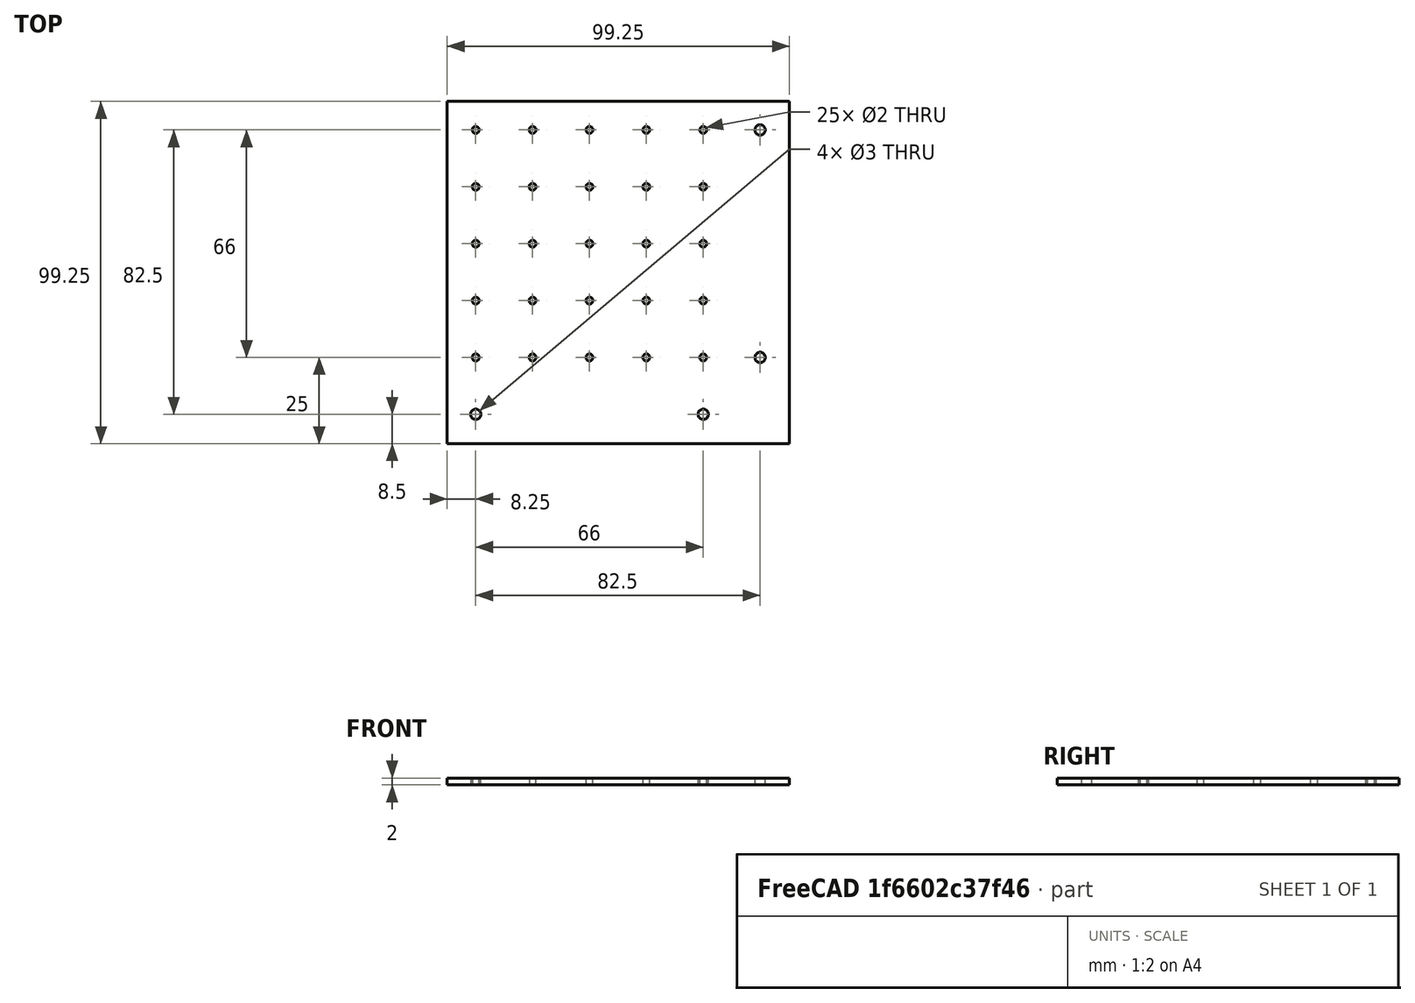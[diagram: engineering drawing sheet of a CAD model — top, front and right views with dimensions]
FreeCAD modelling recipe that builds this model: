
FCSTD DOCUMENT  (FreeCAD 0.21R33771 (Git))
Label: led_matrix_drill_frame
License: All rights reserved
LicenseURL: http://en.wikipedia.org/wiki/All_rights_reserved
objects: Sketcher::SketchObject×1, PartDesign::Pad×1, PartDesign::Body×1
note: 4 computed .brp shape members not serialized (recipe doc carries the construction recipe); baked Part::Feature solids carry a one-line shape summary decoded from their .brp

FEATURE [Sketcher::SketchObject] Sketch
  FullyConstrained = true
  MapMode = 5
  Support = -> [XY_Plane]
  sketch-geometry (37):
    g0: GeomPoint X=0 Y=0 Z=0
    g1: Circle CenterX=0 CenterY=0 CenterZ=0 NormalX=0 NormalY=0 NormalZ=1 AngleXU=0 Radius=1
    g2: Circle CenterX=-16.5 CenterY=0 CenterZ=0 NormalX=0 NormalY=0 NormalZ=1 AngleXU=0 Radius=1
    g3: GeomPoint X=4e-16 Y=16.5 Z=0
    g4: Circle CenterX=4e-16 CenterY=16.5 CenterZ=0 NormalX=0 NormalY=0 NormalZ=1 AngleXU=0 Radius=1
    g5: Circle CenterX=-16.5 CenterY=16.5 CenterZ=0 NormalX=0 NormalY=0 NormalZ=1 AngleXU=0 Radius=1
    g6: GeomPoint X=-33 Y=16.5 Z=0
    g7: Circle CenterX=-33 CenterY=16.5 CenterZ=0 NormalX=0 NormalY=0 NormalZ=1 AngleXU=0 Radius=1
    g8: GeomPoint X=33 Y=16.5 Z=0
    g9: Circle CenterX=33 CenterY=16.5 CenterZ=0 NormalX=0 NormalY=0 NormalZ=1 AngleXU=0 Radius=1
    g10: Circle CenterX=16.5 CenterY=16.5 CenterZ=0 NormalX=0 NormalY=0 NormalZ=1 AngleXU=0 Radius=1
    g11: Circle CenterX=-33 CenterY=0 CenterZ=0 NormalX=0 NormalY=0 NormalZ=1 AngleXU=0 Radius=1
    g12: Circle CenterX=16.5 CenterY=0 CenterZ=0 NormalX=0 NormalY=0 NormalZ=1 AngleXU=0 Radius=1
    g13: Circle CenterX=33 CenterY=0 CenterZ=0 NormalX=0 NormalY=0 NormalZ=1 AngleXU=0 Radius=1
    g14: Circle CenterX=0 CenterY=-16.5 CenterZ=0 NormalX=0 NormalY=0 NormalZ=1 AngleXU=0 Radius=1
    g15: Circle CenterX=16.5 CenterY=-16.5 CenterZ=0 NormalX=0 NormalY=0 NormalZ=1 AngleXU=0 Radius=1
    g16: Circle CenterX=33 CenterY=-16.5 CenterZ=0 NormalX=0 NormalY=0 NormalZ=1 AngleXU=0 Radius=1
    g17: Circle CenterX=-16.5 CenterY=-16.5 CenterZ=0 NormalX=0 NormalY=0 NormalZ=1 AngleXU=0 Radius=1
    g18: Circle CenterX=-33 CenterY=-16.5 CenterZ=0 NormalX=0 NormalY=0 NormalZ=1 AngleXU=0 Radius=1
    g19: Circle CenterX=-33 CenterY=33 CenterZ=0 NormalX=0 NormalY=0 NormalZ=1 AngleXU=0 Radius=1
    g20: Circle CenterX=-16.5 CenterY=33 CenterZ=0 NormalX=0 NormalY=0 NormalZ=1 AngleXU=0 Radius=1
    g21: Circle CenterX=0 CenterY=33 CenterZ=0 NormalX=0 NormalY=0 NormalZ=1 AngleXU=0 Radius=1
    g22: Circle CenterX=16.5 CenterY=33 CenterZ=0 NormalX=0 NormalY=0 NormalZ=1 AngleXU=0 Radius=1
    g23: Circle CenterX=33 CenterY=33 CenterZ=0 NormalX=0 NormalY=0 NormalZ=1 AngleXU=0 Radius=1
    g24: Circle CenterX=-33 CenterY=-33 CenterZ=0 NormalX=0 NormalY=0 NormalZ=1 AngleXU=0 Radius=1
    g25: Circle CenterX=-16.5 CenterY=-33 CenterZ=0 NormalX=0 NormalY=0 NormalZ=1 AngleXU=0 Radius=1
    g26: Circle CenterX=16.5 CenterY=-33 CenterZ=0 NormalX=0 NormalY=0 NormalZ=1 AngleXU=0 Radius=1
    g27: Circle CenterX=33 CenterY=-33 CenterZ=0 NormalX=0 NormalY=0 NormalZ=1 AngleXU=0 Radius=1
    g28: Circle CenterX=0 CenterY=-33 CenterZ=0 NormalX=0 NormalY=0 NormalZ=1 AngleXU=0 Radius=1
    g29: Circle CenterX=-33 CenterY=-49.5 CenterZ=0 NormalX=0 NormalY=0 NormalZ=1 AngleXU=0 Radius=1.5
    g30: Circle CenterX=33 CenterY=-49.5 CenterZ=0 NormalX=0 NormalY=0 NormalZ=1 AngleXU=0 Radius=1.5
    g31: Circle CenterX=49.5 CenterY=33 CenterZ=0 NormalX=0 NormalY=0 NormalZ=1 AngleXU=0 Radius=1.5
    g32: Circle CenterX=49.5 CenterY=-33 CenterZ=0 NormalX=0 NormalY=0 NormalZ=1 AngleXU=0 Radius=1.5
    g33: LineSegment StartX=-41.25 StartY=41.25 StartZ=0 EndX=58 EndY=41.25 EndZ=0
    g34: LineSegment StartX=58 StartY=41.25 StartZ=0 EndX=58 EndY=-58 EndZ=0
    g35: LineSegment StartX=58 StartY=-58 StartZ=0 EndX=-41.25 EndY=-58 EndZ=0
    g36: LineSegment StartX=-41.25 StartY=-58 StartZ=0 EndX=-41.25 EndY=41.25 EndZ=0
  constraints (102):
    c: Coincident(g0,g-1)
    c: Coincident(g1,g0)
    c: Diameter(g1) = 2
    c: PointOnObject(g2,g-1)
    c: Diameter(g2) = 2
    c: Distance(g2,g1) = 16.5
    c: Coincident(g4,g3)
    c: Equal(g1,g4) = 2
    c: Equal(g2,g5) = 2
    c: Distance(g5,g4) = 16.5
    c: Coincident(g7,g6)
    c: Equal(g4,g7) = 2
    c: Distance(g7,g5) = 16.5
    c: Coincident(g9,g8)
    c: Distance(g10,g9) = 16.5
    c: Distance(g10,g4) = 16.5
    c: Distance(g4,g-1) = 16.5
    c: Distance(g5,g-1) = 16.5
    c: Distance(g7,g-1) = 16.5
    c: Distance(g9,g-1) = 16.5
    c: Distance(g10,g-1) = 16.5
    c: Diameter(g10) = 2
    c: Diameter(g9) = 2
    c: PointOnObject(g11,g-1)
    c: Diameter(g11) = 2
    c: Distance(g11,g2) = 16.5
    c: PointOnObject(g12,g-1)
    c: Diameter(g12) = 2
    c: Distance(g12,g-2) = 16.5
    c: PointOnObject(g13,g-1)
    c: Diameter(g13) = 2
    c: Distance(g13,g12) = 16.5
    c: PointOnObject(g14,g-2)
    c: Diameter(g14) = 2
    c: Distance(g14,g1) = 16.5
    c: PointOnObject(g21,g-2)
    c: Diameter(g19) = 2
    c: Diameter(g20) = 2
    c: Diameter(g21) = 2
    c: Diameter(g22) = 2
    c: Diameter(g23) = 2
    c: Diameter(g18) = 2
    c: Diameter(g17) = 2
    c: Diameter(g15) = 2
    c: Diameter(g16) = 2
    c: Diameter(g27) = 2
    c: Diameter(g26) = 2
    c: Diameter(g25) = 2
    c: Diameter(g24) = 2
    c: PointOnObject(g28,g-2)
    c: Diameter(g28) = 2
    c: Distance(g17,g-1) = 16.5
    c: Distance(g17,g-2) = 16.5
    c: Distance(g18,g-1) = 16.5
    c: Distance(g18,g17) = 16.5
    c: Distance(g15,g-2) = 16.5
    c: Distance(g15,g-1) = 16.5
    c: Distance(g16,g-1) = 16.5
    c: Distance(g16,g15) = 16.5
    c: Distance(g28,g14) = 16.5
    c: Distance(g26,g28) = 16.5
    c: Distance(g26,g15) = 16.5
    c: Distance(g27,g26) = 16.5
    c: Distance(g27,g16) = 16.5
    c: Distance(g25,g28) = 16.5
    c: Distance(g25,g17) = 16.5
    c: Distance(g24,g25) = 16.5
    c: Distance(g24,g18) = 16.5
    c: Distance(g19,g7) = 16.5
    c: Distance(g21,g4) = 16.5
    c: Distance(g20,g5) = 16.5
    c: Distance(g20,g-2) = 16.5
    c: Distance(g19,g20) = 16.5
    c: Distance(g22,g10) = 16.5
    c: Distance(g22,g21) = 16.5
    c: Distance(g23,g9) = 16.5
    c: Distance(g23,g22) = 16.5
    c: Distance(g7,g-2) = 33
    c: Diameter(g31) = 3
    c: Diameter(g32) = 3
    c: Diameter(g30) = 3
    c: Diameter(g29) = 3
    c: Distance(g29,g-2) = 33
    c: Distance(g29,g24) = 16.5
    c: Distance(g30,g-2) = 33
    c: Distance(g30,g27) = 16.5
    c: Distance(g32,g-1) = 33
    c: Distance(g32,g27) = 16.5
    c: Distance(g31,g-1) = 33
    c: Distance(g31,g23) = 16.5
    c: Coincident(g33,g34)
    c: Coincident(g34,g35)
    c: Coincident(g35,g36)
    c: Coincident(g36,g33)
    c: Horizontal(g33)
    c: Horizontal(g35)
    c: Vertical(g34)
    c: Vertical(g36)
    c: Distance(g35,g-2) = 41.25
    c: Distance(g33,g-1) = 41.25
    c: Distance(g34,g-2) = 58
    c: Distance(g34,g-1) = 58
FEATURE [PartDesign::Pad] Pad
  Direction = (0,0,1)
  Length = 2
  Length2 = 10
  Profile = -> Sketch
  ReferenceAxis = -> Sketch [N_Axis]
  Type = 0
FEATURE [PartDesign::Body] Body
  Group = -> [Sketch,Pad]
  Origin = -> Origin
  Tip = -> Pad
